# Revit family: Plumbing_Drainage_hansgrohe_56029USA-RainDrain-Rock-Finish-set-showe_NEW
name_source: partatom
category: Plumbing Fixtures
revit_build: Autodesk Revit 2018 (Build: 20170223_1515(x64)
units: mm (PartAtom-declared; Revit-internal decimal feet)

## family parameters
Cut with Voids When Loaded = No
Host = Face
OmniClass Number = 23.31.17.29
OmniClass Title = Shower Drains
Part Type = Normal
Room Calculation Point = No
Round Connector Dimension = Use Diameter
Shared = No

## types (1)
- 56029USA RainDrain Rock Finish set shower drain 600 cuttable and tileable
    BIMobject category = Drainage
    Default Elevation = 48"
    Description = RainDrain Rock Finish set shower drain 600 cuttable and tileable
    Design country = Germany
    EAN code = 4059625430651
    Edition number = 1
    IFC Classification = Pipe Fitting
    Manufacturer = Hansgrohe
    Manufacturer country = Germany
    Manufacturer name = hansgrohe
    Masterformat 2014 Code = 22 13 19.13
    Masterformat 2014 Description = Sanitary Drains
    Material = Hansgrohe - Metal - Stainless Steel
    Material 1 = Hansgrohe - Plastic - Black
    Model = 56029USA
    OmniClass Code = 23-31 17 29
    OmniClass Description = Shower Drains
    Product Guid = a277dc4b-2b08-4384-9a1f-51b054a9ca78
    Product SKU = 56029USA
    Product data url = https://bimobject.com
    Product family = Finish sets shower drains
    Product group = RainDrain Rock
    Product name = 56029USA RainDrain Rock Finish set shower drain 600 cuttable and tileable
    Product url = https://pro.hansgrohe.com
    QR code = https://bimobject.com
    UNSPSC Code = 40141719
    URL = https://www.hansgrohe.com
    Uniclass 2015 Code = Pr_65_52_25
    Uniclass 2015 Name = Drainage traps and accessories
    Uniformat II Code = D2010
    Uniformat II Description = Plumbing Fixtures
    Version = 1
    Weight Net (Kg) = 0.4

## geometry (parser evidence)
native form markers: Sweep x2
no freeform markers — native parametric forms only
